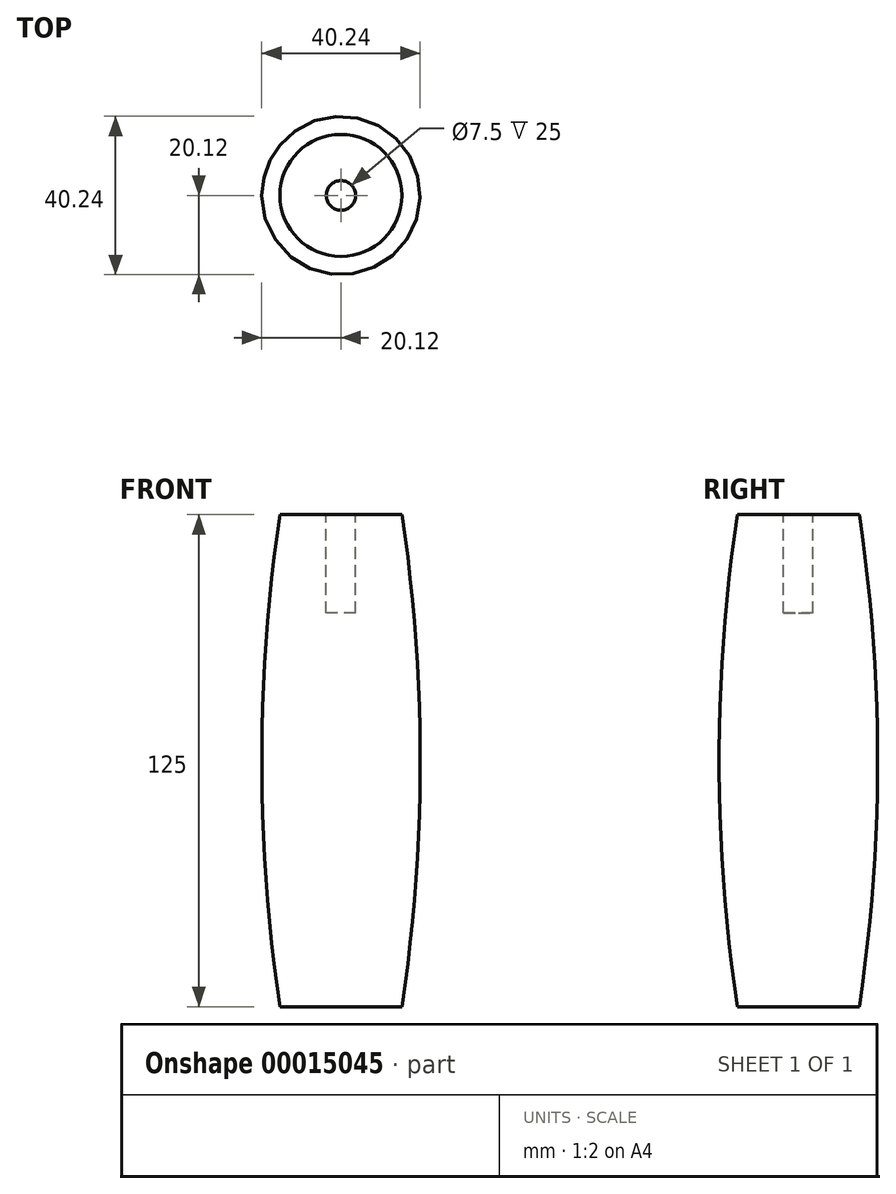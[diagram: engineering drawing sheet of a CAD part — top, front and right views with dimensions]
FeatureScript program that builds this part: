
annotation { "Feature Type Name" : "Feature", "Feature Type Description" : "" }
export const myFeature = defineFeature(function(context is Context, id is Id, definition is map)
    precondition{}
    {
        {
            var Q0;
            Q0=qCreatedBy(makeId("Front.planeOp"),FACE);
            var sketch = newSketch(context, id + "F0", { "sketchPlane" : qUnion([Q0])});
            skLineSegment(sketch, "E0", {"start": v(0, 0) * mm, "end": v(0, 125) * mm});
            skLineSegment(sketch, "E1.0", {"start": v(15.5, 0) * mm, "end": v(15.5, 125) * mm});
            skArc(sketch, "E2", {"start": v(15.5, 0) * mm, "mid": v(20.12, 62.5) * mm, "end": v(15.5, 125) * mm});
            skLineSegment(sketch, "E3", {"start": v(15.5, 125) * mm, "end": v(0, 125) * mm});
            skLineSegment(sketch, "E4", {"start": v(15.5, 0) * mm, "end": v(0, 0) * mm});
            skSolve(sketch);
        }
        {
            var Q0;
            Q0 = qSketchRegion(id + "F0", true);
            var Q1;
            Q1=sQuery(id+"F0.wireOp",EDGE,"E0");
            revolve(context, id + "F1", {"entities" : qUnion([Q0]), "axis" : qUnion([Q1]), "revolveType" : RevolveType.FULL});
        }
        {
            var Q0;
            Q0=makeQuery(id+"F1.opRevolve","SWEPT_FACE",FACE,{"disambiguationData":[OSD([sQuery(id+"F0.wireOp",EDGE,"E3")])]});
            var sketch = newSketch(context, id + "F2", { "sketchPlane" : qUnion([Q0])});
            skCircle(sketch, "E5", {"center": v(0, 0) * mm, "radius": 3.75 * mm});
            skSolve(sketch);
        }
        {
            var Q0;
            Q0 = qSketchRegion(id + "F2", true);
            extrude(context, id + "F3", {"entities" : qUnion([Q0]), "operationType" : NewBodyOperationType.REMOVE, "oppositeDirection" : true, "depth" : 25 * mm});
        }
    });
